# Revit family: CBS4LEDS-DIF-xx-xx_V1.0_Non-Hosted_R16
name_source: partatom
category: Lighting Fixtures
revit_build: Autodesk Revit 2016 (Build: 20151007_0715(x64)
units: mm (PartAtom-declared; Revit-internal decimal feet)

## family parameters
Always vertical = Yes
Cut with Voids When Loaded = No
Light Source = Yes
OmniClass Number = 23.80.70.00
OmniClass Title = Lighting
Part Type = Normal
Room Calculation Point = No
Round Connector Dimension = Use Diameter
Shared = No
Work Plane-Based = No

## types (5) — shared parameters
AS2293 Classification = C0=D40 C90=D40
Battery = 3.2V 3200mAh
Battery Type = Lithium Iron Phosphate
Charging Method = Intelligent Current Limited Constant Voltage
Color Filter = 16777215
Construction = Powder coated steel body
Diffuser = Acrylic prismatic diffuser
Dimming Lamp Color Temperature Shift = <None>
Emit Shape Visible in Rendering = No
Emit from Rectangle Length = 1219 mm
Emit from Rectangle Width = 610 mm
IP Rating = IP20
Manufacturer = Clevertronics
Mounting = Surface mount
Operating Mode = Sustained
Operating Temperature = 1˚C to 40˚C
Photometric Web File = ll22528_CBS4LEDS-DIF-ZW(AUB02110010002,AS2293.3,Photometry).ies
Power factor = 0.95
Replacement Battery = 1550050 Battery, LP 3.2V 3200mAh 70mm lead, no Bracket
Replacement Lamp = 8002695 PCA:LED Strip 8S6P, ALS-13-840-0-02-B
Tilt Angle = 90.00°
Weight = 3.3Kg

## per-type parameters (varying)
| type | Description | Dimensions (L x W x H) | LED Driver | Lamp | MIC Number | Operating Voltage | Power Consumption | Power Consumption (Standby) | Product Description | Replacement Driver | Replacement Emergency Driver | Testing Node | Testing System | Total Lumen Output | Type Comments |
| CBS4LEDS-DIF-DD-HV | LP Premium Odyssey Quantum LED Diffused Batten with LED Emergency Pod and Dali
Driver | 1271mm x 120mm x 108mm | DALI Driver: 50W 350-1050mA | LED strip module, 50000h life | AUB02810170001 | 220-240V AC; 50Hz | 44W (Max charging, Lamp ON), 40W (Standby, Lamp ON) | 1.3W (Lamp OFF) | LP Premium Odyssey Quantum LED Diffused Batten with LED Emergency Pod and Dali
Driver | 1330056 LED Driver - LCA 50w 350-1050mA,ONEFORALL | CLIFE-CKIT-HV-NP Lifelight, Control Only, HV, LP, OWC, 650mA (incl. HIVE Node) | 8001390 RF Node CT10678-Ax Internal Antenna | Zoneworks XT HIVE (RF) | 4585lm @ 118lm /W | LP Premium Odyssey Quantum LED Diffused Batten with LED Emergency Pod and Dali |
| CBS4LEDS-DIF | LP Premium Quantum LED diffused batten with LED Emergency Pod
Driver | 1271mm x 120mm x 108mm | 50W 700mA, XZ-STB50, 50,000hr | LED strip module, 4,000K natural white, 50,000h life [L70/B50 Ta 40°C], Ra>80 | AUB02310010001 | 240V AC; 50Hz | 38 Watts (Lamps ON) | 1.0 Watts (Lamps OFF) | LP Premium Quantum LED diffused batten with LED Emergency Pod
Driver | 1330059 LED XZ Driver - 50w 700mA, 30-54V | CLIFE-CKIT-NP Lifelight, Control Only, LP, No Plug |  | Clevertest Plus Enabled (Not activated by default) | 4585lm @121lm/W (123lm/W for non-EM version) | LP Premium Quantum LED diffused batten with LED Emergency Pod |
| CBS4LEDS-DIF-ZW | LP Premium Quantum LED diffused batten with LED Emergency Pod | 1274mm x 120mm x 110mm | 50w 700mA, XZ-STB50, 50,000hr | LED strip module, 4,000K natural white, 50,000h life [L70/B50 Ta 40°C], Ra>80 | AUB02110010001 | 240V AC; 50Hz | 38 Watts (Lamps ON) | 1.0 Watts (Lamps OFF) | LP Premium Quantum LED diffused batten with LED Emergency Pod
Driver | 1330059 LED XZ Driver – 50w 700mA, 30-54V | CLIFE-CKIT-NP Lifelight, Control Only, LP, No Plug | 8001450 PCA:Powerline Node ZW, #CT10310-A6 | Zoneworks computerised testing | 4585lm @121lm/W (123lm/W for non-EM version) | LLP Premium Quantum LED diffused batten with LED Emergency Pod |
| CBS4LEDS-DIF-DALI | LP Premium Quantum 1200mm LED Diffused Batten with LED Emergency Pod | 1271mm x 120mm x 108mm | LED XZ Driver – 50w 700mA, 30-54V | LED Strip Module, 4,000K Natural White, 50,000h Life [L70/B50 Ta 40°C], Ra>80 | AUB02210990002 | 240V AC; 50Hz | 39W (Lamps ON) | 0.4W (Lamps OFF, Standby) | LP Premium Quantum 1200mm LED Diffused Batten with LED Emergency Pod | 1330059 LED XZ Driver – 50w 700mA, 30-54V | CLIFE-CKIT-DALI-NP  Lifelight, Control Only,Dali Reg, LP,No Plug |  | DALI Registered | 4585lm @115lm/W | LP Premium Quantum 1200mm LED Diffused Batten with LED Emergency Pod |
| CBS4LEDS-DIF-HV | LP Premium Quantum LED Diffused Batten with LED Emergency Pod
Driver | 1271mm x 120mm x 108mm | LED XZ Driver – 50w 700mA, 30-54V | LED Strip Module, 4,000K Natural White, 50,000h Life [L70/B50 Ta 40°C], Ra>80 | AUB02810040001 | 220-240V AC; 50Hz | 39W | 0.4W | LP Premium Quantum LED Diffused Batten with LED Emergency Pod
Driver | 1330059 LED XZ Driver – 50w 700mA, 30-54V | CLIFE-CKIT-NP Lifelight, Control Only, LP, No Plug | 8001390 RF Node CT10678-Ax Internal Antenna | Zoneworks XT HIVE (RF) | 4585lm @115lm/W | LP Premium Quantum LED Diffused Batten with LED Emergency Pod |

note: column(s) folded — value = type name in every type: Model

## geometry (parser evidence)
native form markers: Sweep x3
no freeform markers — native parametric forms only
